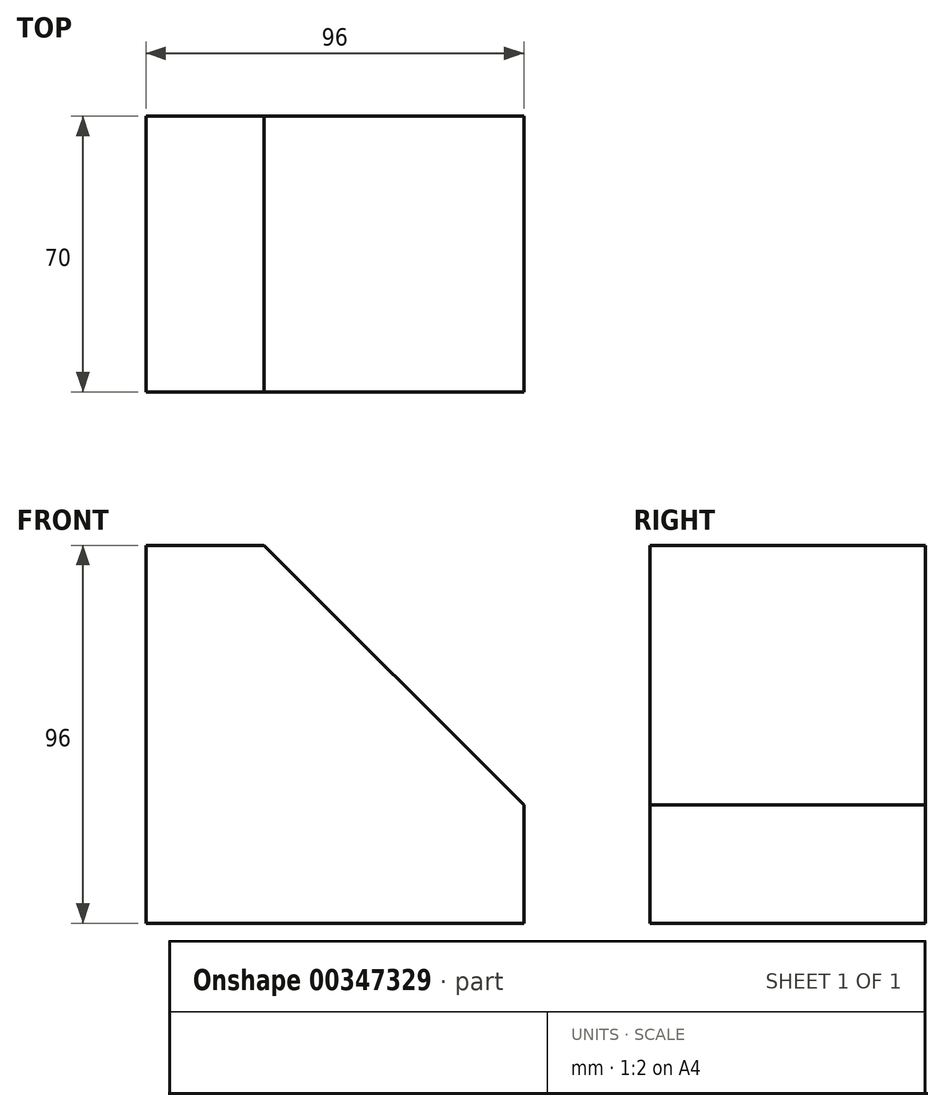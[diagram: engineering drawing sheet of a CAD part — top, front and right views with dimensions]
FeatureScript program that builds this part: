
annotation { "Feature Type Name" : "Feature", "Feature Type Description" : "" }
export const myFeature = defineFeature(function(context is Context, id is Id, definition is map)
    precondition{}
    {
        {
            var Q0;
            Q0=qCreatedBy(makeId("Top.planeOp"),FACE);
            var sketch = newSketch(context, id + "F0", { "sketchPlane" : qUnion([Q0])});
            skLineSegment(sketch, "E0.bottom", {"start": v(48, 35) * mm, "end": v(-48, 35) * mm});
            skLineSegment(sketch, "E0.top", {"start": v(48, -35) * mm, "end": v(-48, -35) * mm});
            skLineSegment(sketch, "E0.left", {"start": v(48, 35) * mm, "end": v(48, -35) * mm});
            skLineSegment(sketch, "E0.right", {"start": v(-48, 35) * mm, "end": v(-48, -35) * mm});
            skPoint(sketch, "E0.middle", {"position": v(0, 0) * mm});
            skSolve(sketch);
        }
        {
            var Q0;
            Q0 = qSketchRegion(id + "F0", true);
            extrude(context, id + "F1", {"entities" : qUnion([Q0]), "depth" : 96 * mm});
        }
        {
            var Q0;
            Q0=makeQuery(id+"F1.opExtrude","CAP_EDGE",EDGE,{"disambiguationData":[OSD([sQuery(id+"F0.wireOp",EDGE,"E0.left")])],"isStart":false});
            chamfer(context, id + "F2", {"entities" : qUnion([Q0]), "width" : 66 * mm, "tangentPropagation" : true});
        }
    });
